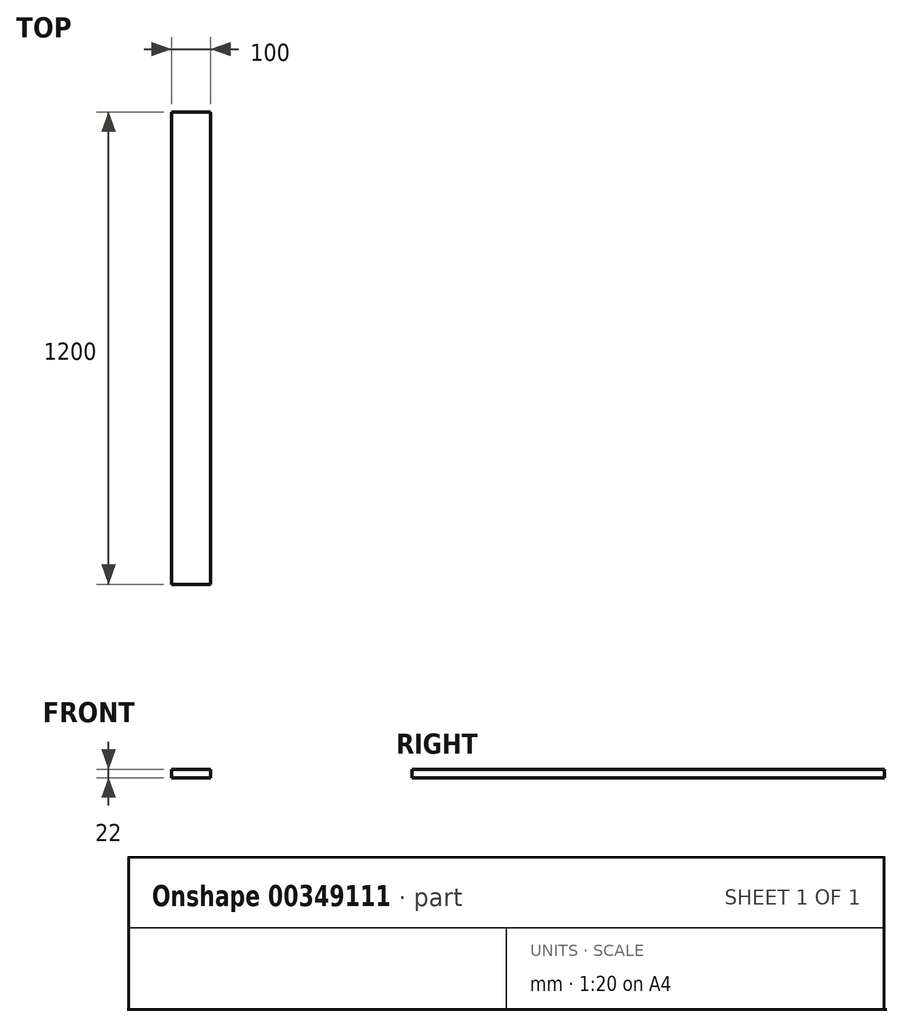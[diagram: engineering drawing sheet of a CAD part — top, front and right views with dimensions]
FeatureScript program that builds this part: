
annotation { "Feature Type Name" : "Feature", "Feature Type Description" : "" }
export const myFeature = defineFeature(function(context is Context, id is Id, definition is map)
    precondition{}
    {
        {
            var Q0;
            Q0=qCreatedBy(makeId("Top.planeOp"),FACE);
            var sketch = newSketch(context, id + "F0", { "sketchPlane" : qUnion([Q0])});
            skLineSegment(sketch, "E0.bottom", {"start": v(50, -600) * mm, "end": v(-50, -600) * mm});
            skLineSegment(sketch, "E0.top", {"start": v(50, 600) * mm, "end": v(-50, 600) * mm});
            skLineSegment(sketch, "E0.left", {"start": v(50, -600) * mm, "end": v(50, 600) * mm});
            skLineSegment(sketch, "E0.right", {"start": v(-50, -600) * mm, "end": v(-50, 600) * mm});
            skSolve(sketch);
        }
        {
            var Q0;
            Q0 = qSketchRegion(id + "F0", true);
            extrude(context, id + "F1", {"entities" : qUnion([Q0]), "endBound" : BoundingType.SYMMETRIC, "depth" : 22 * mm});
        }
    });
